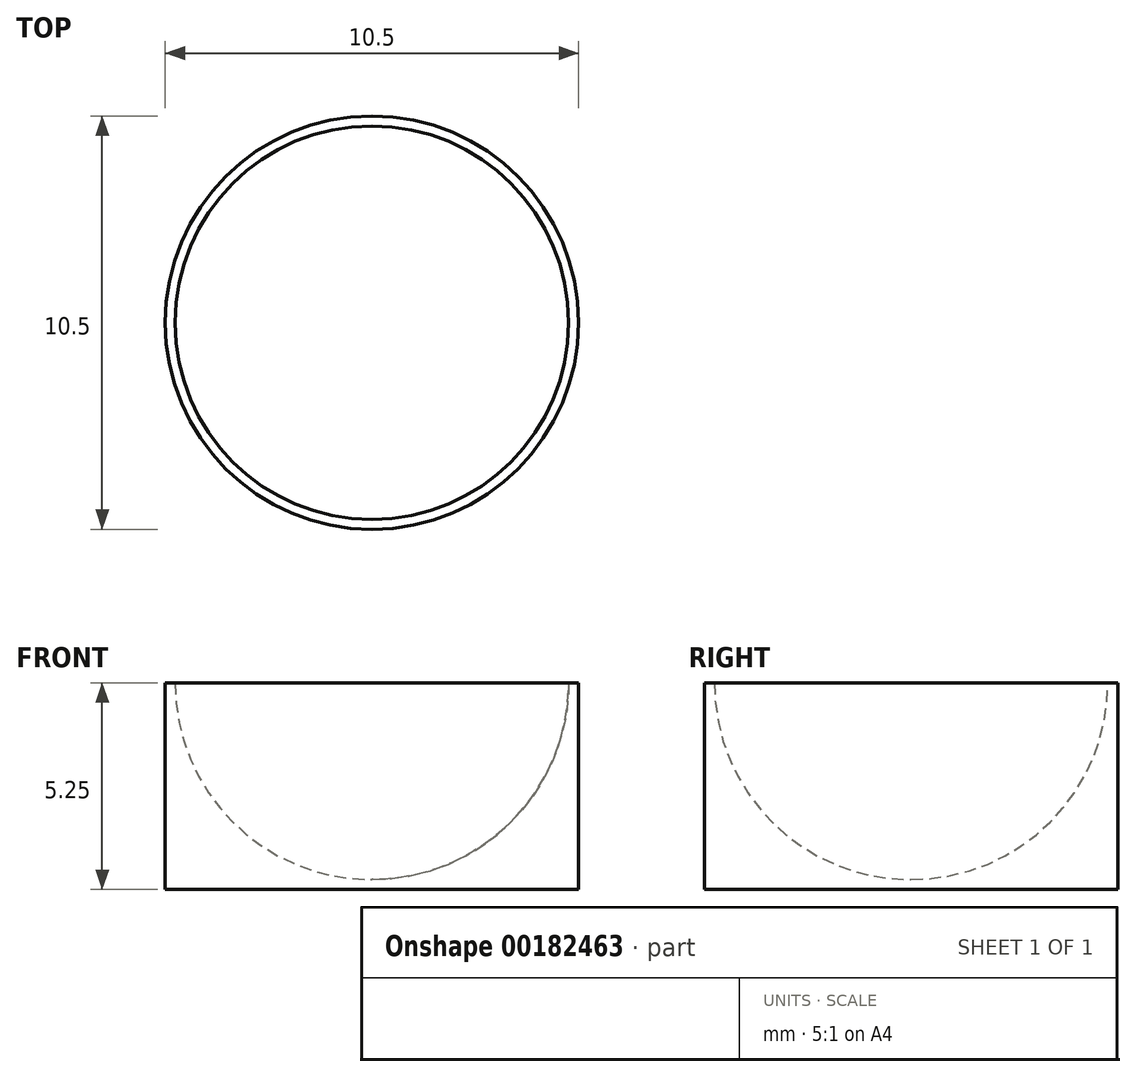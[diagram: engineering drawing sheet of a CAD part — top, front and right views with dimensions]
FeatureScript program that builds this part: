
annotation { "Feature Type Name" : "Feature", "Feature Type Description" : "" }
export const myFeature = defineFeature(function(context is Context, id is Id, definition is map)
    precondition{}
    {
        {
            var Q0;
            Q0=qCreatedBy(makeId("Front.planeOp"),FACE);
            var sketch = newSketch(context, id + "F0", { "sketchPlane" : qUnion([Q0])});
            skLineSegment(sketch, "E0", {"start": v(0, 0) * mm, "end": v(5, 0) * mm});
            skLineSegment(sketch, "E1", {"start": v(5, 0) * mm, "end": v(5, 5) * mm});
            skArc(sketch, "E2", {"start": v(5, 5) * mm, "mid": v(3.54, 1.46) * mm, "end": v(0, 0) * mm});
            skLineSegment(sketch, "E3", {"start": v(5, 5) * mm, "end": v(0, 5) * mm, "construction": true});
            skLineSegment(sketch, "E4", {"start": v(0, 0) * mm, "end": v(0, 5) * mm, "construction": true});
            skLineSegment(sketch, "E5", {"start": v(0, 0) * mm, "end": v(0, -0.25) * mm});
            skLineSegment(sketch, "E6", {"start": v(0, -0.25) * mm, "end": v(5.25, -0.25) * mm});
            skLineSegment(sketch, "E7", {"start": v(5.25, -0.25) * mm, "end": v(5.25, 5) * mm});
            skLineSegment(sketch, "E8", {"start": v(5.25, 5) * mm, "end": v(5, 5) * mm});
            skSolve(sketch);
        }
        {
            var Q0;
            Q0=makeQuery(id+"F0.imprint","IMPRINT",FACE,{"disambiguationData":[TD([[makeQuery(id+"F0.imprint","IMPRINT",EDGE,{"derivedFrom":sQuery(id+"F0.wireOp",EDGE,"E0")}),1.0]])]});
            var Q1;
            Q1=makeQuery(id+"F0.imprint","IMPRINT",FACE,{"disambiguationData":[TD([[makeQuery(id+"F0.imprint","IMPRINT",EDGE,{"derivedFrom":sQuery(id+"F0.wireOp",EDGE,"E0")}),-1.0]])]});
            var Q2;
            Q2=sQuery(id+"F0.wireOp",EDGE,"E4");
            revolve(context, id + "F1", {"entities" : qUnion([Q0, Q1]), "axis" : qUnion([Q2]), "revolveType" : RevolveType.FULL});
        }
    });
